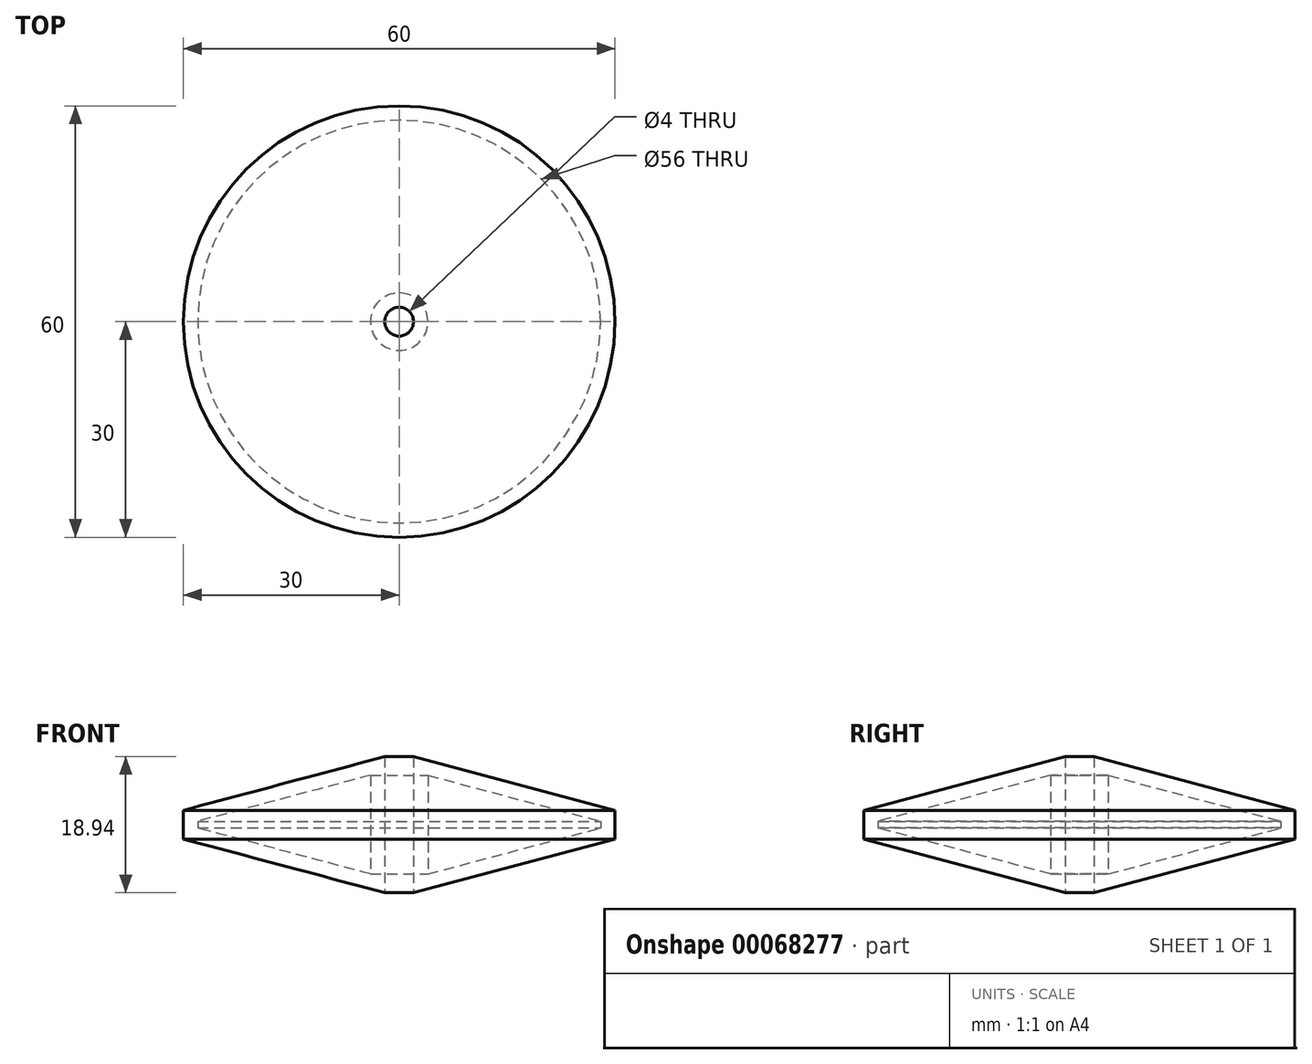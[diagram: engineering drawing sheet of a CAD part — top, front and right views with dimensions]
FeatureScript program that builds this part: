
annotation { "Feature Type Name" : "Feature", "Feature Type Description" : "" }
export const myFeature = defineFeature(function(context is Context, id is Id, definition is map)
    precondition{}
    {
        {
            var Q0;
            Q0=qCreatedBy(makeId("Front.planeOp"),FACE);
            var sketch = newSketch(context, id + "F0", { "sketchPlane" : qUnion([Q0])});
            skLineSegment(sketch, "E0", {"start": v(0, 0) * mm, "end": v(0, 10) * mm});
            skLineSegment(sketch, "E1", {"start": v(0, 10) * mm, "end": v(30, 2) * mm});
            skLineSegment(sketch, "E2", {"start": v(30, 2) * mm, "end": v(30, 0) * mm});
            skLineSegment(sketch, "E3", {"start": v(30, 0) * mm, "end": v(0, 0) * mm});
            skSolve(sketch);
        }
        {
            var Q0;
            Q0=makeQuery(id+"F0.imprint","IMPRINT",FACE,{"disambiguationData":[TD([[makeQuery(id+"F0.imprint","IMPRINT",EDGE,{"derivedFrom":sQuery(id+"F0.wireOp",EDGE,"E0")}),-1.0]])]});
            var Q1;
            Q1=sQuery(id+"F0.wireOp",EDGE,"E0");
            revolve(context, id + "F1", {"entities" : qUnion([Q0]), "axis" : qUnion([Q1]), "revolveType" : RevolveType.FULL});
        }
        {
            var Q0;
            Q0=qCreatedBy(makeId("Top.planeOp"),FACE);
            var sketch = newSketch(context, id + "F2", { "sketchPlane" : qUnion([Q0])});
            skLineSegment(sketch, "E4", {"start": v(0, -13.42) * mm, "end": v(0, 13.8) * mm, "construction": true});
            skLineSegment(sketch, "E5", {"start": v(0, 13.8) * mm, "end": v(13.52, 0) * mm, "construction": true});
            skLineSegment(sketch, "E6", {"start": v(13.52, 0) * mm, "end": v(0, 0) * mm, "construction": true});
            skSolve(sketch);
        }
        {
            var Q0;
            Q0=sQuery(id+"F2.wireOp",VERTEX,"E6.end");
            var Q1;
            Q1=makeQuery(id+"F1.opRevolve","SWEPT_BODY",BODY,{"disambiguationData":[OSD([sQuery(id+"F0.wireOp",EDGE,"E0"),sQuery(id+"F0.wireOp",EDGE,"E1"),sQuery(id+"F0.wireOp",EDGE,"E2"),sQuery(id+"F0.wireOp",EDGE,"E3")])]});
            hole(context, id + "F3", {"style" : HoleStyle.SIMPLE, "holeDiameter" : 4 * mm, "endStyle" : HoleEndStyle.THROUGH, "oppositeDirection" : true, "locations" : qUnion([Q0]), "scope" : qUnion([Q1]), "isTappedThrough" : true});
        }
        {
            var Q0;
            Q0=makeQuery(id+"F1.opRevolve","SWEPT_FACE",FACE,{"disambiguationData":[OSD([sQuery(id+"F0.wireOp",EDGE,"E3")])]});
            shell(context, id + "F4", {"entities" : qUnion([Q0]), "thickness" : 2 * mm});
        }
        {
            var Q0;
            Q0=makeQuery(id+"F1.opRevolve","SWEPT_BODY",BODY,{"disambiguationData":[OSD([sQuery(id+"F0.wireOp",EDGE,"E0"),sQuery(id+"F0.wireOp",EDGE,"E1"),sQuery(id+"F0.wireOp",EDGE,"E2"),sQuery(id+"F0.wireOp",EDGE,"E3")])]});
            var Q1;
            Q1=qCreatedBy(makeId("Top.planeOp"),FACE);
            mirror(context, id + "F5", {"operationType" : NewBodyOperationType.ADD, "entities" : qUnion([Q0]), "mirrorPlane" : qUnion([Q1])});
        }
    });
